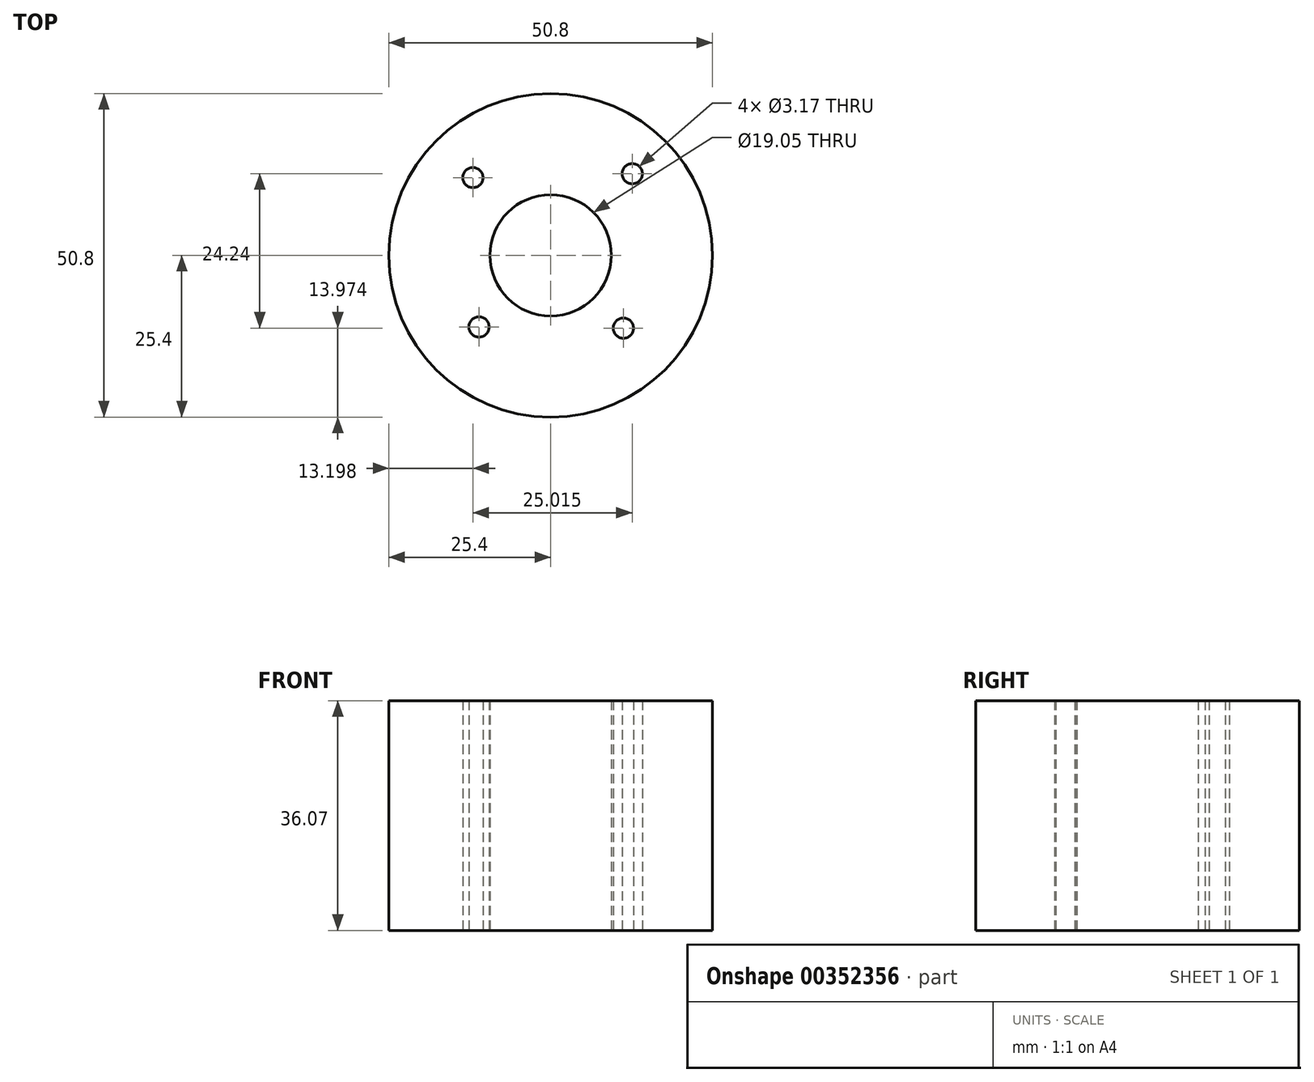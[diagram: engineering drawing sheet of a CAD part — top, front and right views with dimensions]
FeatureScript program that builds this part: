
annotation { "Feature Type Name" : "Feature", "Feature Type Description" : "" }
export const myFeature = defineFeature(function(context is Context, id is Id, definition is map)
    precondition{}
    {
        {
            var Q0;
            Q0=qCreatedBy(makeId("Top.planeOp"),FACE);
            var sketch = newSketch(context, id + "F0", { "sketchPlane" : qUnion([Q0])});
            skCircle(sketch, "E0", {"center": v(0, 0) * mm, "radius": 25.4 * mm});
            skLineSegment(sketch, "E1", {"start": v(0, 0) * mm, "end": v(25.4, 0) * mm});
            skCircle(sketch, "E2", {"center": v(0, 0) * mm, "radius": 9.53 * mm});
            skLineSegment(sketch, "E3", {"start": v(0, 0) * mm, "end": v(12.81, 12.81) * mm});
            skLineSegment(sketch, "E4", {"start": v(0, 0) * mm, "end": v(11.43, -11.43) * mm});
            skLineSegment(sketch, "E5", {"start": v(0, 0) * mm, "end": v(-12.2, 12.2) * mm});
            skLineSegment(sketch, "E6", {"start": v(0, 0) * mm, "end": v(-11.24, -11.24) * mm});
            skCircle(sketch, "E7", {"center": v(12.81, 12.81) * mm, "radius": 1.59 * mm});
            skPoint(sketch, "E8.perimeterSnap0", {"position": v(5.71, -5.71) * mm});
            skCircle(sketch, "E9", {"center": v(-12.2, 12.2) * mm, "radius": 1.59 * mm});
            skCircle(sketch, "E10", {"center": v(-11.24, -11.24) * mm, "radius": 1.59 * mm});
            skCircle(sketch, "E11", {"center": v(11.43, -11.43) * mm, "radius": 1.59 * mm});
            skSolve(sketch);
        }
        {
            var Q0;
            Q0=makeQuery(id+"F0.imprint","IMPRINT",FACE,{"disambiguationData":[TD([[makeQuery(id+"F0.imprint","IMPRINT",EDGE,{"derivedFrom":sQuery(id+"F0.wireOp",EDGE,"E0")}),1.0]])]});
            extrude(context, id + "F1", {"entities" : qUnion([Q0]), "depth" : 36.07 * mm});
        }
    });
